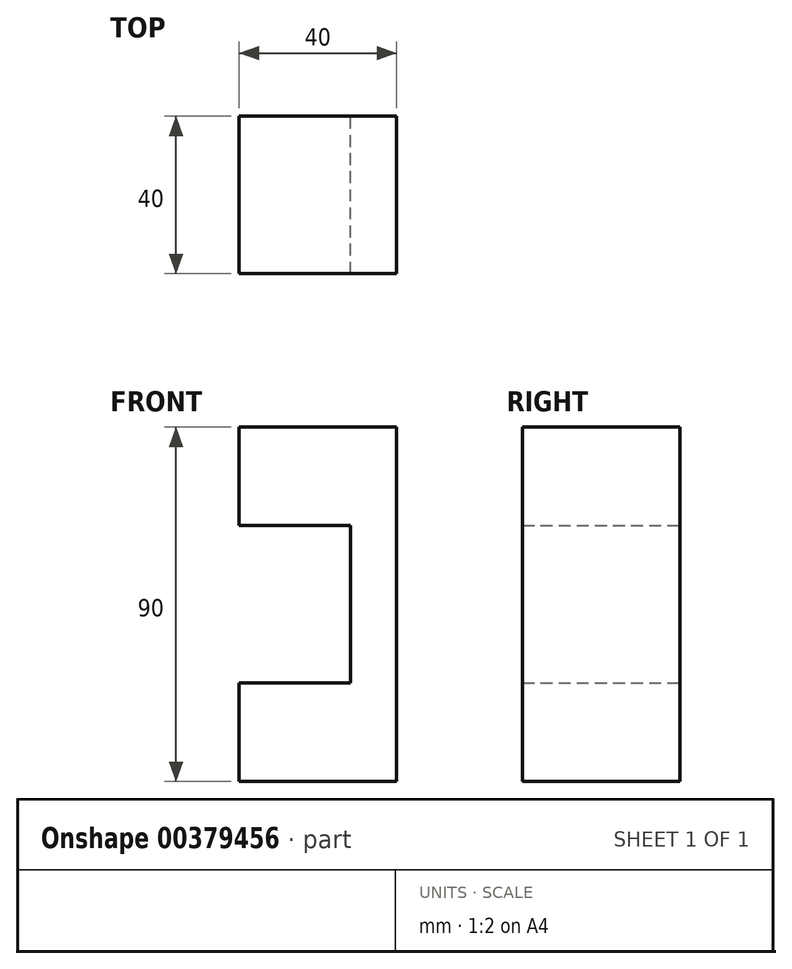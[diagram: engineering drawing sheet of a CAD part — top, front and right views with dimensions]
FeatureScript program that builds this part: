
annotation { "Feature Type Name" : "Feature", "Feature Type Description" : "" }
export const myFeature = defineFeature(function(context is Context, id is Id, definition is map)
    precondition{}
    {
        {
            var Q0;
            Q0=qCreatedBy(makeId("Front.planeOp"),FACE);
            var sketch = newSketch(context, id + "F0", { "sketchPlane" : qUnion([Q0])});
            skLineSegment(sketch, "E0.bottom", {"start": v(0, 0) * mm, "end": v(-40, 0) * mm});
            skLineSegment(sketch, "E0.top", {"start": v(0, -25) * mm, "end": v(-40, -25) * mm});
            skLineSegment(sketch, "E0.left", {"start": v(0, 0) * mm, "end": v(0, -25) * mm});
            skLineSegment(sketch, "E0.right", {"start": v(-40, 0) * mm, "end": v(-40, -25) * mm});
            skLineSegment(sketch, "E1", {"start": v(-11.75, 0) * mm, "end": v(-11.75, 40) * mm});
            skLineSegment(sketch, "E2.bottom", {"start": v(0, 40) * mm, "end": v(-40, 40) * mm});
            skLineSegment(sketch, "E2.top", {"start": v(0, 65) * mm, "end": v(-40, 65) * mm});
            skLineSegment(sketch, "E2.left", {"start": v(0, 40) * mm, "end": v(0, 65) * mm});
            skLineSegment(sketch, "E2.right", {"start": v(-40, 40) * mm, "end": v(-40, 65) * mm});
            skLineSegment(sketch, "E3", {"start": v(0, 40) * mm, "end": v(0, 0) * mm});
            skSolve(sketch);
        }
        {
            var Q0;
            Q0=makeQuery(id+"F0.imprint","IMPRINT",FACE,{"disambiguationData":[TD([[makeQuery(id+"F0.imprint","IMPRINT",EDGE,{"derivedFrom":sQuery(id+"F0.wireOp",EDGE,"E2.top")}),1.0]])]});
            var Q1;
            {var subQ2=sQuery(id+"F0.wireOp",EDGE,"E1");Q1=makeQuery(id+"F0.imprint","IMPRINT",FACE,{"disambiguationData":[TD([[makeQuery(id+"F0.imprint","IMPRINT",EDGE,{"derivedFrom":subQ2}),-1.0]])]});}
            var Q2;
            Q2=makeQuery(id+"F0.imprint","IMPRINT",FACE,{"disambiguationData":[TD([[makeQuery(id+"F0.imprint","IMPRINT",EDGE,{"derivedFrom":sQuery(id+"F0.wireOp",EDGE,"E0.top")}),-1.0]])]});
            extrude(context, id + "F1", {"entities" : qUnion([Q0, Q1, Q2]), "depth" : 40 * mm});
        }
    });
